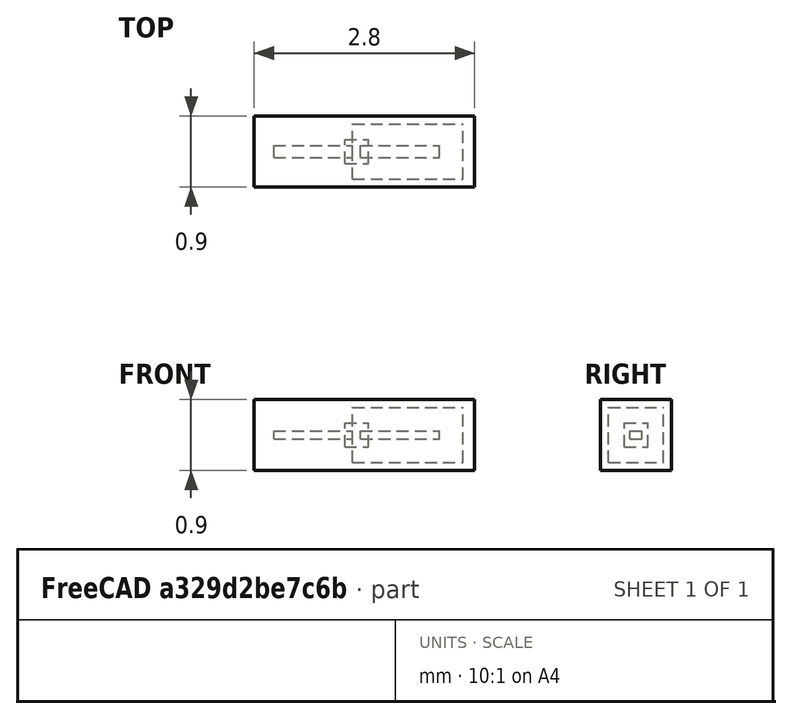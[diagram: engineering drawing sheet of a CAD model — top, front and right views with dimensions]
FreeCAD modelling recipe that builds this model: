
FCSTD DOCUMENT  (FreeCAD 1.0R39109 (Git))
Label: model
License: All rights reserved
LicenseURL: https://en.wikipedia.org/wiki/All_rights_reserved
objects: Part::Feature×6, Part::Box×5, Part::FeaturePython×4, App::DocumentObjectGroupPython×2
note: 15 computed .brp shape members not serialized (recipe doc carries the construction recipe); baked Part::Feature solids carry a one-line shape summary decoded from their .brp

FEATURE [Part::Box] Box  label="hullWall1"
  AttacherType = Attacher::AttachEngine3D
  Height = 0.1
  Length = 1
  Placement = pos=(0,-0.075,-0.05) rot=(0,0,1;0rad)
  Width = 0.15
FEATURE [Part::Box] Box001  label="hullWall2"
  AttacherType = Attacher::AttachEngine3D
  Height = 0.1
  Length = 1
  Placement = pos=(-1.1,-0.075,-0.05) rot=(0,0,1;0rad)
  Width = 0.15
FEATURE [Part::Feature] Face  label="outlet"
  Placement = pos=(-1.5,-0.5,-0.5) rot=(0,0,1;0rad)
  shape: bbox 2e-07 x 1 x 1 mm, 1 faces, 0 solids (baked)
FEATURE [Part::Feature] Face001  label="inlet"
  Placement = pos=(-1.5,-0.5,-0.5) rot=(0,0,1;0rad)
  shape: bbox 2e-07 x 1 x 1 mm, 1 faces, 0 solids (baked)
FEATURE [Part::Feature] Face002  label="front"
  Placement = pos=(-1.5,-0.5,-0.5) rot=(0,0,1;0rad)
  shape: bbox 5 x 2e-07 x 1 mm, 1 faces, 0 solids (baked)
FEATURE [Part::Feature] Face003  label="back"
  Placement = pos=(-1.5,-0.5,-0.5) rot=(0,0,1;0rad)
  shape: bbox 5 x 2e-07 x 1 mm, 1 faces, 0 solids (baked)
FEATURE [Part::Feature] Face004  label="base"
  Placement = pos=(-1.5,-0.5,-0.5) rot=(0,0,1;0rad)
  shape: bbox 5 x 1 x 2e-07 mm, 1 faces, 0 solids (baked)
FEATURE [Part::Feature] Face005  label="atomosphere"
  Placement = pos=(-1.5,-0.5,-0.5) rot=(0,0,1;0rad)
  shape: bbox 5 x 1 x 2e-07 mm, 1 faces, 0 solids (baked)
FEATURE [Part::Box] Box002  label="overset1"
  AttacherType = Attacher::AttachEngine3D
  Height = 0.7
  Length = 1.4
  Placement = pos=(-0.1,-0.35,-0.35) rot=(0,0,1;0rad)
  Width = 0.7
FEATURE [Part::Box] Box003  label="overset2"
  AttacherType = Attacher::AttachEngine3D
  Height = 0.9
  Length = 2.8
  Placement = pos=(-1.35,-0.45,-0.45) rot=(0,0,1;0rad)
  Width = 0.9
FEATURE [Part::FeaturePython] CfdSolver  # WARN: FeaturePython — macro-defined, semantics opaque (R4)
  Parallel = true
  ParallelCores = 1
  ParallelMethod = 0
FEATURE [Part::FeaturePython] MeshRefinement  # WARN: FeaturePython — macro-defined, semantics opaque (R4)
  AllowDiscont = true
  CellSize = 0.051
  ExpansionRatio = 1.2
  FirstLayerHeight = 0
  Internal = false
  KeepCell = false
  NumberLayers = 1
  RefinementLevel = 0
  RefinementThickness = 0
  RemoveCell = false
  ShapeRefs = -> [Box001]
  patchType = 1
FEATURE [Part::FeaturePython] MeshRefinement001  # WARN: FeaturePython — macro-defined, semantics opaque (R4)
  AllowDiscont = true
  CellSize = 0.051
  ExpansionRatio = 1.2
  FirstLayerHeight = 0
  Internal = false
  KeepCell = false
  NumberLayers = 1
  RefinementLevel = 0
  RefinementThickness = 0
  RemoveCell = false
  ShapeRefs = -> [Box003]
  patchType = 3
FEATURE [Part::Box] Box004  label="fineRegion"
  AttacherType = Attacher::AttachEngine3D
  Height = 0.3
  Length = 0.3
  Placement = pos=(-0.2,-0.15,-0.15) rot=(0,0,1;0rad)
  Width = 0.3
FEATURE [Part::FeaturePython] MeshRefinement002  # WARN: FeaturePython — macro-defined, semantics opaque (R4)
  AllowDiscont = true
  CellSize = 0.0075
  ExpansionRatio = 1.2
  FirstLayerHeight = 0
  Internal = true
  KeepCell = false
  NumberLayers = 1
  RefinementLevel = 1
  RefinementThickness = 0
  RemoveCell = false
  ShapeRefs = -> [Box004]
  patchType = 0
FEATURE [App::DocumentObjectGroupPython] CFDMesh  # scripted group (container) (typed FeaturePython)
  BaseCellSize = 0.025
  ElementDimension = 1
  FeatureAngle = 30
  Group = -> [MeshRefinement,MeshRefinement001,MeshRefinement002]
  MeshUtility = 0
  ScaleToMeter = 1
  keepCellsIntersectingBoundary = false
  opt_featureSizeFactor = 0.4
  opt_maxNumIterations = 5
  opt_nSmoothNormals = 3
  opt_reCalculateNormals = true
  opt_relThicknessTol = 0.05
  optimiseLayer = false
  patchTypeSetting = false
  workflowControls = 0
FEATURE [App::DocumentObjectGroupPython] dexcsCfdAnalysis  # scripted group (container) (typed FeaturePython)
  Group = -> [CFDMesh,CfdSolver]
  IsActiveAnalysis = true
  NeedsCaseRewrite = true
  NeedsMeshRerun = true
  NeedsMeshRewrite = true
  PlotMaxnumber = 5000
  PlotMethodLast = false
